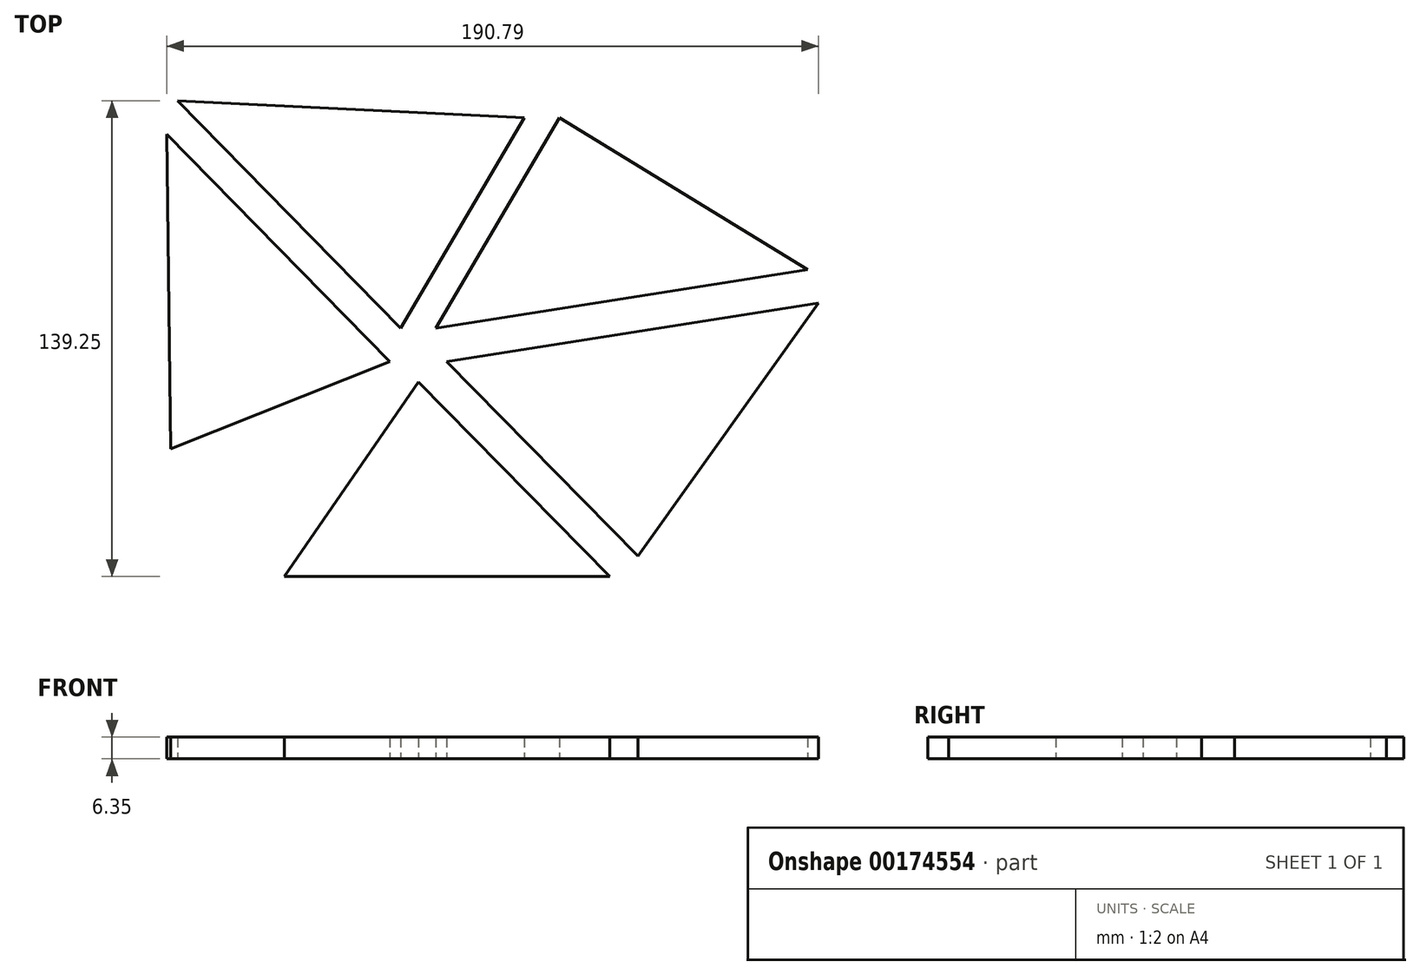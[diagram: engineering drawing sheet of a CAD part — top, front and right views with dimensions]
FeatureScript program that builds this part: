
annotation { "Feature Type Name" : "Feature", "Feature Type Description" : "" }
export const myFeature = defineFeature(function(context is Context, id is Id, definition is map)
    precondition{}
    {
        {
            var Q0;
            Q0=qCreatedBy(makeId("Top.planeOp"),FACE);
            var sketch = newSketch(context, id + "F0", { "sketchPlane" : qUnion([Q0])});
            skCircle(sketch, "E0.cCircle", {"center": v(0, 0) * mm, "radius": 8.74 * mm, "construction": true});
            skLineSegment(sketch, "E0.0", {"start": v(6.35, -8.74) * mm, "end": v(-6.35, -8.74) * mm, "construction": true});
            skLineSegment(sketch, "E0.1", {"start": v(-6.35, -8.74) * mm, "end": v(-10.27, 3.34) * mm, "construction": true});
            skLineSegment(sketch, "E0.2", {"start": v(-10.27, 3.34) * mm, "end": v(0, 10.8) * mm, "construction": true});
            skLineSegment(sketch, "E0.3", {"start": v(0, 10.8) * mm, "end": v(10.27, 3.34) * mm, "construction": true});
            skLineSegment(sketch, "E0.4", {"start": v(10.27, 3.34) * mm, "end": v(6.35, -8.74) * mm, "construction": true});
            skPoint(sketch, "E0.0.midPoint", {"position": v(0, -8.74) * mm});
            skLineSegment(sketch, "E1", {"start": v(-5.14, 7.07) * mm, "end": v(31.05, 68.6) * mm});
            skLineSegment(sketch, "E2", {"start": v(31.05, 68.6) * mm, "end": v(-70.43, 73.6) * mm});
            skLineSegment(sketch, "E3", {"start": v(-70.43, 73.6) * mm, "end": v(-5.14, 7.07) * mm});
            skLineSegment(sketch, "E4", {"start": v(-8.31, -2.7) * mm, "end": v(-73.6, 63.84) * mm});
            skLineSegment(sketch, "E5", {"start": v(-73.6, 63.84) * mm, "end": v(-72.54, -28.23) * mm});
            skLineSegment(sketch, "E6", {"start": v(-72.54, -28.23) * mm, "end": v(-8.31, -2.7) * mm});
            skLineSegment(sketch, "E7", {"start": v(0, -8.74) * mm, "end": v(-39.23, -65.64) * mm});
            skLineSegment(sketch, "E8", {"start": v(-39.23, -65.64) * mm, "end": v(56.02, -65.64) * mm});
            skLineSegment(sketch, "E9", {"start": v(56.02, -65.64) * mm, "end": v(0, -8.74) * mm});
            skLineSegment(sketch, "E10", {"start": v(8.31, -2.7) * mm, "end": v(64.33, -59.6) * mm});
            skLineSegment(sketch, "E11", {"start": v(64.33, -59.6) * mm, "end": v(117.19, 14.4) * mm});
            skLineSegment(sketch, "E12", {"start": v(117.19, 14.4) * mm, "end": v(8.31, -2.7) * mm});
            skLineSegment(sketch, "E13", {"start": v(5.14, 7.07) * mm, "end": v(41.33, 68.6) * mm});
            skLineSegment(sketch, "E14", {"start": v(41.33, 68.6) * mm, "end": v(114.01, 24.16) * mm});
            skLineSegment(sketch, "E15", {"start": v(114.01, 24.16) * mm, "end": v(5.14, 7.07) * mm});
            skSolve(sketch);
        }
        {
            var Q0;
            Q0=qCreatedBy(makeId("Top.planeOp"),FACE);
            var sketch = newSketch(context, id + "F1", { "sketchPlane" : qUnion([Q0])});
            skLineSegment(sketch, "E16.0.0", {"start": v(-72.54, -28.23) * mm, "end": v(-8.31, -2.7) * mm});
            skLineSegment(sketch, "E16.0.1", {"start": v(-8.31, -2.7) * mm, "end": v(-73.6, 63.84) * mm});
            skLineSegment(sketch, "E16.0.2", {"start": v(-73.6, 63.84) * mm, "end": v(-72.54, -28.23) * mm});
            skLineSegment(sketch, "E17.0.0", {"start": v(-70.43, 73.6) * mm, "end": v(-5.14, 7.07) * mm});
            skLineSegment(sketch, "E17.0.1", {"start": v(-5.14, 7.07) * mm, "end": v(31.05, 68.6) * mm});
            skLineSegment(sketch, "E17.0.2", {"start": v(31.05, 68.6) * mm, "end": v(-70.43, 73.6) * mm});
            skLineSegment(sketch, "E18.0.0", {"start": v(41.33, 68.6) * mm, "end": v(5.14, 7.07) * mm});
            skLineSegment(sketch, "E18.0.1", {"start": v(5.14, 7.07) * mm, "end": v(114.01, 24.16) * mm});
            skLineSegment(sketch, "E18.0.2", {"start": v(114.01, 24.16) * mm, "end": v(41.33, 68.6) * mm});
            skLineSegment(sketch, "E19.0.0", {"start": v(117.19, 14.4) * mm, "end": v(8.31, -2.7) * mm});
            skLineSegment(sketch, "E19.0.1", {"start": v(8.31, -2.7) * mm, "end": v(64.33, -59.6) * mm});
            skLineSegment(sketch, "E19.0.2", {"start": v(64.33, -59.6) * mm, "end": v(117.19, 14.4) * mm});
            skLineSegment(sketch, "E20.0.0", {"start": v(56.02, -65.64) * mm, "end": v(0, -8.74) * mm});
            skLineSegment(sketch, "E20.0.1", {"start": v(0, -8.74) * mm, "end": v(-39.23, -65.64) * mm});
            skLineSegment(sketch, "E20.0.2", {"start": v(-39.23, -65.64) * mm, "end": v(56.02, -65.64) * mm});
            skSolve(sketch);
        }
        {
            var Q0;
            Q0 = qSketchRegion(id + "F1", true);
            extrude(context, id + "F2", {"entities" : qUnion([Q0]), "depth" : 6.35 * mm});
        }
    });
